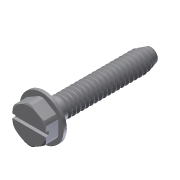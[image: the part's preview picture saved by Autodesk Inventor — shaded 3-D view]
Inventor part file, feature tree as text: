
AUTODESK INVENTOR PART (.ipt)
format: ipt  version: 2011 (Build 150239000, 239)  size: 623,104 bytes
history: native  units: in
note: dims shown in document units (in); Inventor stores cm internally (conversion verified against a paired STEP export)
features: other x1, imported_body x1, extrude x1, sketch x1
ambient origin geometry x8: Origin, YZ Plane, XZ Plane, XY Plane, X Axis, Y Axis, Z Axis, Center Point
feature tree (4):
  parser-record x1  (decoder bookkeeping rows leaked as tree rows — omitted from the tree; the rows remain in map.json)
  imported_body  "Base1"
  extrude  "Extrusion1"  Depth=0.125in TaperAngle=0.0deg
  sketch  "Sketch1"  dims[d0=0.19in d1=0.125in d2=0.0in]
